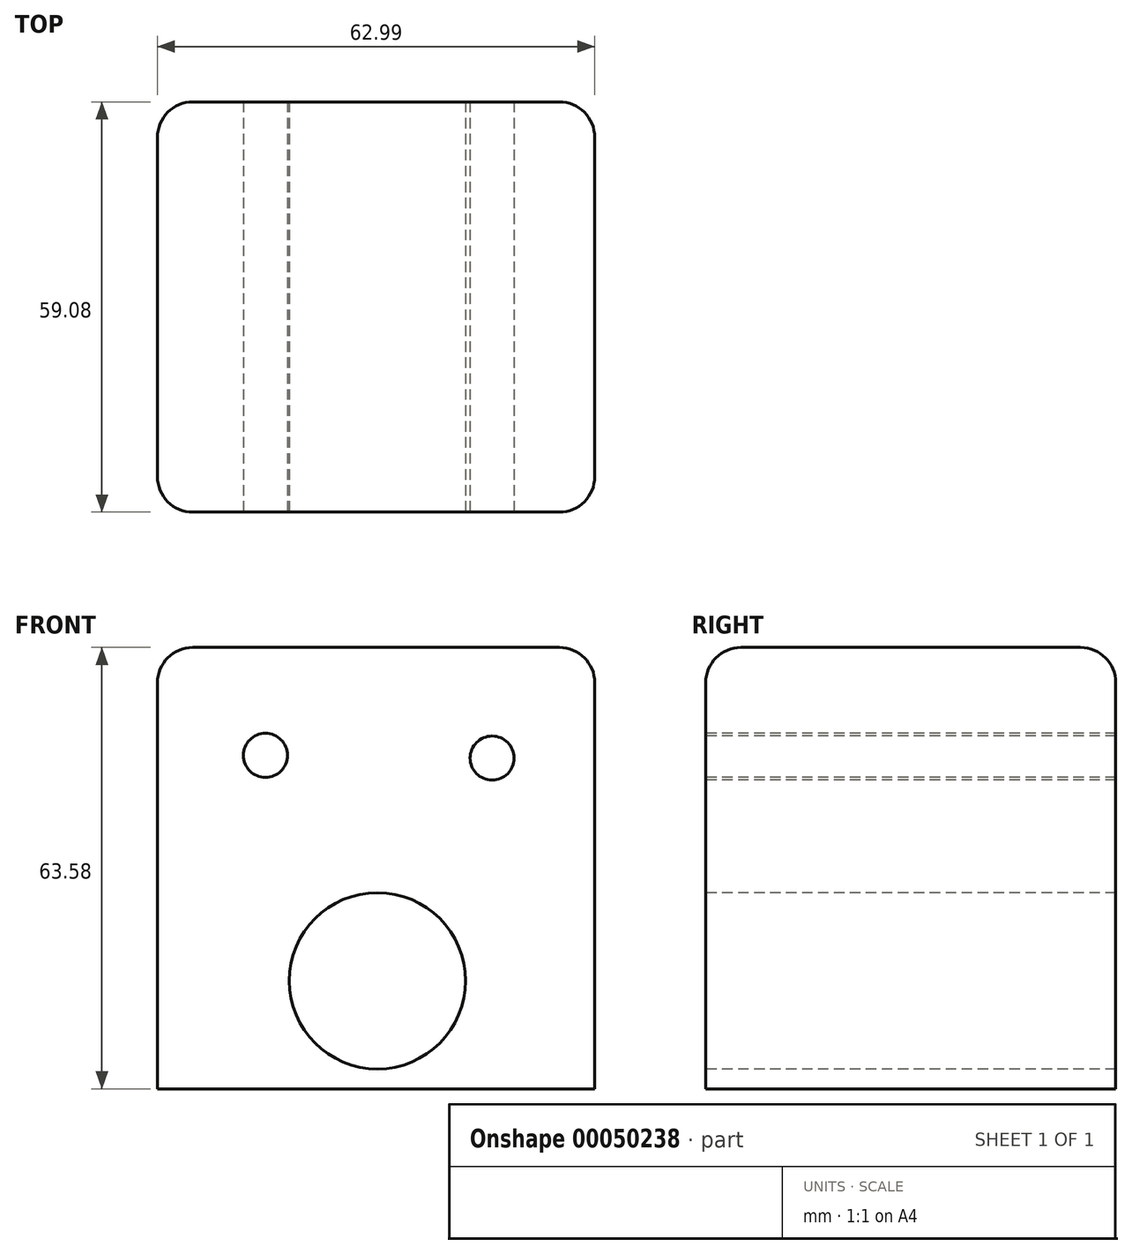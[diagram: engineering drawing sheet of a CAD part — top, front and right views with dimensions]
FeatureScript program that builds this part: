
annotation { "Feature Type Name" : "Feature", "Feature Type Description" : "" }
export const myFeature = defineFeature(function(context is Context, id is Id, definition is map)
    precondition{}
    {
        {
            var Q0;
            Q0=qCreatedBy(makeId("Front.planeOp"),FACE);
            var sketch = newSketch(context, id + "F0", { "sketchPlane" : qUnion([Q0])});
            skLineSegment(sketch, "E0.bottom", {"start": v(-23.33, 24.01) * mm, "end": v(39.66, 24.01) * mm});
            skLineSegment(sketch, "E0.top", {"start": v(-23.33, -39.57) * mm, "end": v(39.66, -39.57) * mm});
            skLineSegment(sketch, "E0.left", {"start": v(-23.33, 24.01) * mm, "end": v(-23.33, -39.57) * mm});
            skLineSegment(sketch, "E0.right", {"start": v(39.66, 24.01) * mm, "end": v(39.66, -39.57) * mm});
            skSolve(sketch);
        }
        {
            var Q0;
            Q0 = qSketchRegion(id + "F0", true);
            extrude(context, id + "F1", {"entities" : qUnion([Q0]), "oppositeDirection" : true, "depth" : 59.08 * mm});
        }
        {
            var Q0;
            Q0=makeQuery(id+"F1.opExtrude","CAP_EDGE",EDGE,{"disambiguationData":[OSD([sQuery(id+"F0.wireOp",EDGE,"E0.left")])],"isStart":true});
            var Q1;
            Q1=makeQuery(id+"F1.opExtrude","CAP_EDGE",EDGE,{"disambiguationData":[OSD([sQuery(id+"F0.wireOp",EDGE,"E0.bottom")])],"isStart":true});
            var Q2;
            Q2=makeQuery(id+"F1.opExtrude","SWEPT_EDGE",EDGE,{"disambiguationData":[OSD([sQuery(id+"F0.wireOp",EDGE,"E0.bottom"),sQuery(id+"F0.wireOp",EDGE,"E0.left")])]});
            var Q3;
            Q3=makeQuery(id+"F1.opExtrude","CAP_EDGE",EDGE,{"disambiguationData":[OSD([sQuery(id+"F0.wireOp",EDGE,"E0.bottom")])],"isStart":false});
            var Q4;
            Q4=makeQuery(id+"F1.opExtrude","CAP_EDGE",EDGE,{"disambiguationData":[OSD([sQuery(id+"F0.wireOp",EDGE,"E0.left")])],"isStart":false});
            var Q5;
            Q5=makeQuery(id+"F1.opExtrude","SWEPT_EDGE",EDGE,{"disambiguationData":[OSD([sQuery(id+"F0.wireOp",EDGE,"E0.bottom"),sQuery(id+"F0.wireOp",EDGE,"E0.right")])]});
            var Q6;
            Q6=makeQuery(id+"F1.opExtrude","CAP_EDGE",EDGE,{"disambiguationData":[OSD([sQuery(id+"F0.wireOp",EDGE,"E0.right")])],"isStart":false});
            var Q7;
            Q7=makeQuery(id+"F1.opExtrude","CAP_EDGE",EDGE,{"disambiguationData":[OSD([sQuery(id+"F0.wireOp",EDGE,"E0.right")])],"isStart":true});
            fillet(context, id + "F2", {"entities" : qUnion([Q0, Q1, Q2, Q3, Q4, Q5, Q6, Q7]), "radius" : 5.08 * mm, "tangentPropagation" : true, "allowEdgeOverflow" : false});
        }
        {
            var Q0;
            Q0=qCreatedBy(makeId("Front.planeOp"),FACE);
            var sketch = newSketch(context, id + "F3", { "sketchPlane" : qUnion([Q0])});
            skCircle(sketch, "E1", {"center": v(-7.78, 8.46) * mm, "radius": 7.05 * mm});
            skCircle(sketch, "E2", {"center": v(24.89, 8.07) * mm, "radius": 7.14 * mm});
            skCircle(sketch, "E3", {"center": v(8.36, -24.01) * mm, "radius": 14.8 * mm});
            skSolve(sketch);
        }
        {
            var Q0;
            Q0=sQuery(id+"F3.wireOp",VERTEX,"E1.center");
            var Q1;
            Q1=sQuery(id+"F3.wireOp",VERTEX,"E2.center");
            var Q2;
            Q2=makeQuery(id+"F1.opExtrude","SWEPT_BODY",BODY,{"disambiguationData":[OSD([sQuery(id+"F0.wireOp",EDGE,"E0.bottom"),sQuery(id+"F0.wireOp",EDGE,"E0.top"),sQuery(id+"F0.wireOp",EDGE,"E0.left"),sQuery(id+"F0.wireOp",EDGE,"E0.right")])]});
            hole(context, id + "F4", {"style" : HoleStyle.SIMPLE, "holeDiameter" : 6.35 * mm, "endStyle" : HoleEndStyle.THROUGH, "locations" : qUnion([Q0, Q1]), "scope" : qUnion([Q2])});
        }
        {
            var Q0;
            Q0=sQuery(id+"F3.wireOp",VERTEX,"E3.center");
            var Q1;
            Q1=makeQuery(id+"F1.opExtrude","SWEPT_BODY",BODY,{"disambiguationData":[OSD([sQuery(id+"F0.wireOp",EDGE,"E0.bottom"),sQuery(id+"F0.wireOp",EDGE,"E0.top"),sQuery(id+"F0.wireOp",EDGE,"E0.left"),sQuery(id+"F0.wireOp",EDGE,"E0.right")])]});
            hole(context, id + "F5", {"style" : HoleStyle.SIMPLE, "holeDiameter" : 25.4 * mm, "endStyle" : HoleEndStyle.THROUGH, "locations" : qUnion([Q0]), "scope" : qUnion([Q1])});
        }
    });
